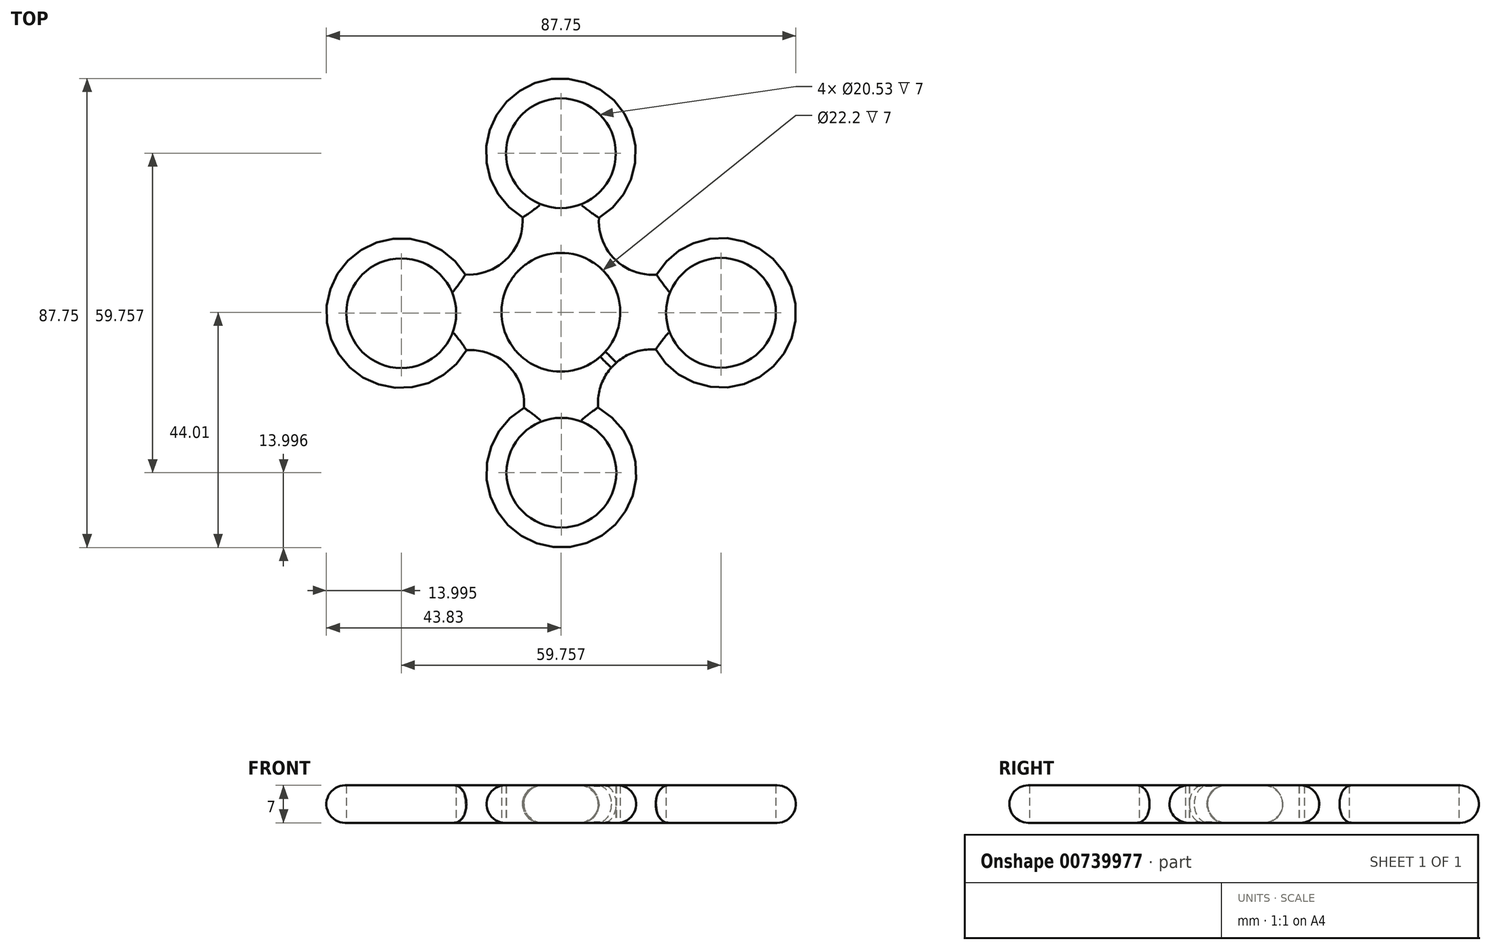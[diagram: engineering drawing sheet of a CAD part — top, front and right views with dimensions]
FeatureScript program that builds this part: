
annotation { "Feature Type Name" : "Feature", "Feature Type Description" : "" }
export const myFeature = defineFeature(function(context is Context, id is Id, definition is map)
    precondition{}
    {
        {
            var Q0;
            Q0=qCreatedBy(makeId("Top.planeOp"),FACE);
            var sketch = newSketch(context, id + "F0", { "sketchPlane" : qUnion([Q0])});
            skCircle(sketch, "E0", {"center": v(0, 0) * mm, "radius": 11.1 * mm});
            skLineSegment(sketch, "E1", {"start": v(0, 11.1) * mm, "end": v(0, 16.1) * mm});
            skCircle(sketch, "E2", {"center": v(0, 29.74) * mm, "radius": 10.26 * mm});
            skCircle(sketch, "E3.1.0", {"center": v(-29.83, -0.18) * mm, "radius": 10.26 * mm});
            skCircle(sketch, "E3.2.0", {"center": v(0.09, -30.01) * mm, "radius": 10.26 * mm});
            skCircle(sketch, "E3.3.0", {"center": v(29.92, -0.1) * mm, "radius": 10.26 * mm});
            skPoint(sketch, "E3.center", {"position": v(0.04, -0.14) * mm});
            skCircle(sketch, "E4", {"center": v(0, 29.74) * mm, "radius": 14 * mm});
            skCircle(sketch, "E5", {"center": v(29.92, -0.1) * mm, "radius": 14 * mm});
            skCircle(sketch, "E6", {"center": v(0.09, -30.01) * mm, "radius": 14 * mm});
            skCircle(sketch, "E7", {"center": v(-29.83, -0.18) * mm, "radius": 14 * mm});
            skCircle(sketch, "E8", {"center": v(0, 0) * mm, "radius": 14 * mm});
            skArc(sketch, "E9", {"start": v(-6.91, -17.9) * mm, "mid": v(-9.8, -10.02) * mm, "end": v(-17.66, -7.09) * mm});
            skArc(sketch, "E10", {"start": v(-17.85, 7.06) * mm, "mid": v(-10.1, 9.97) * mm, "end": v(-7.18, 17.72) * mm});
            skArc(sketch, "E11", {"start": v(7.11, 17.69) * mm, "mid": v(10.07, 9.92) * mm, "end": v(17.88, 7.05) * mm});
            skArc(sketch, "E12", {"start": v(17.73, -6.97) * mm, "mid": v(9.84, -9.9) * mm, "end": v(6.96, -17.82) * mm});
            skArc(sketch, "E13.trimOffspring", {"start": v(10.14, -27.96) * mm, "mid": v(11.9, -27.26) * mm, "end": v(13.62, -26.44) * mm});
            skSolve(sketch);
        }
        {
            var Q0;
            Q0 = qSketchRegion(id + "F0", true);
            extrude(context, id + "F1", {"entities" : qUnion([Q0]), "depth" : 7 * mm, "offsetDistance" : 25 * mm});
        }
        {
            var Q0;
            {var subQ0=sQuery(id+"F0.wireOp",EDGE,"E12");Q0=makeQuery(id+"F1.opExtrude","CAP_EDGE",EDGE,{"disambiguationData":[OSD([subQ0]),TDD([makeQuery(id+"F0.imprint","IMPRINT",EDGE,{"disambiguationData":[TD([[makeQuery(id+"F0.imprint","INTERSECT",VERTEX,{"derivedFrom":[sQuery(id+"F0.wireOp",EDGE,"E5"),subQ0]}),-1.0]])],"derivedFrom":subQ0})])],"isStart":true});}
            var Q1;
            Q1=makeQuery(id+"F1.opExtrude","CAP_EDGE",EDGE,{"disambiguationData":[OSD([sQuery(id+"F0.wireOp",EDGE,"E5")])],"isStart":true});
            var Q2;
            {var subQ0=sQuery(id+"F0.wireOp",EDGE,"E12");Q2=makeQuery(id+"F1.opExtrude","CAP_EDGE",EDGE,{"disambiguationData":[OSD([subQ0]),TDD([makeQuery(id+"F0.imprint","IMPRINT",EDGE,{"disambiguationData":[TD([[makeQuery(id+"F0.imprint","INTERSECT",VERTEX,{"derivedFrom":[sQuery(id+"F0.wireOp",EDGE,"E6"),subQ0]}),1.0]])],"derivedFrom":subQ0})])],"isStart":true});}
            var Q3;
            Q3=makeQuery(id+"F1.opExtrude","CAP_EDGE",EDGE,{"disambiguationData":[OSD([sQuery(id+"F0.wireOp",EDGE,"E8")])],"isStart":true});
            var Q4;
            Q4=makeQuery(id+"F1.opExtrude","CAP_EDGE",EDGE,{"disambiguationData":[OSD([sQuery(id+"F0.wireOp",EDGE,"E6")])],"isStart":true});
            var Q5;
            Q5=makeQuery(id+"F1.opExtrude","CAP_EDGE",EDGE,{"disambiguationData":[OSD([sQuery(id+"F0.wireOp",EDGE,"E9")])],"isStart":true});
            var Q6;
            Q6=makeQuery(id+"F1.opExtrude","CAP_EDGE",EDGE,{"disambiguationData":[OSD([sQuery(id+"F0.wireOp",EDGE,"E7")])],"isStart":true});
            var Q7;
            Q7=makeQuery(id+"F1.opExtrude","CAP_EDGE",EDGE,{"disambiguationData":[OSD([sQuery(id+"F0.wireOp",EDGE,"E10")])],"isStart":true});
            var Q8;
            Q8=makeQuery(id+"F1.opExtrude","CAP_EDGE",EDGE,{"disambiguationData":[OSD([sQuery(id+"F0.wireOp",EDGE,"E11")])],"isStart":false});
            var Q9;
            Q9=makeQuery(id+"F1.opExtrude","CAP_EDGE",EDGE,{"disambiguationData":[OSD([sQuery(id+"F0.wireOp",EDGE,"E4")])],"isStart":false});
            var Q10;
            Q10=makeQuery(id+"F1.opExtrude","CAP_EDGE",EDGE,{"disambiguationData":[OSD([sQuery(id+"F0.wireOp",EDGE,"E4")])],"isStart":true});
            var Q11;
            Q11=makeQuery(id+"F1.opExtrude","CAP_EDGE",EDGE,{"disambiguationData":[OSD([sQuery(id+"F0.wireOp",EDGE,"E11")])],"isStart":true});
            var Q12;
            Q12=makeQuery(id+"F1.opExtrude","CAP_EDGE",EDGE,{"disambiguationData":[OSD([sQuery(id+"F0.wireOp",EDGE,"E5")])],"isStart":false});
            var Q13;
            Q13=makeQuery(id+"F1.opExtrude","CAP_EDGE",EDGE,{"disambiguationData":[OSD([sQuery(id+"F0.wireOp",EDGE,"E10")])],"isStart":false});
            var Q14;
            Q14=makeQuery(id+"F1.opExtrude","CAP_EDGE",EDGE,{"disambiguationData":[OSD([sQuery(id+"F0.wireOp",EDGE,"E7")])],"isStart":false});
            var Q15;
            Q15=makeQuery(id+"F1.opExtrude","CAP_EDGE",EDGE,{"disambiguationData":[OSD([sQuery(id+"F0.wireOp",EDGE,"E6")])],"isStart":false});
            var Q16;
            Q16=makeQuery(id+"F1.opExtrude","CAP_EDGE",EDGE,{"disambiguationData":[OSD([sQuery(id+"F0.wireOp",EDGE,"E9")])],"isStart":false});
            var Q17;
            {var subQ0=sQuery(id+"F0.wireOp",EDGE,"E12");Q17=makeQuery(id+"F1.opExtrude","CAP_EDGE",EDGE,{"disambiguationData":[OSD([subQ0]),TDD([makeQuery(id+"F0.imprint","IMPRINT",EDGE,{"disambiguationData":[TD([[makeQuery(id+"F0.imprint","INTERSECT",VERTEX,{"derivedFrom":[sQuery(id+"F0.wireOp",EDGE,"E6"),subQ0]}),1.0]])],"derivedFrom":subQ0})])],"isStart":false});}
            var Q18;
            {var subQ0=sQuery(id+"F0.wireOp",EDGE,"E12");Q18=makeQuery(id+"F1.opExtrude","CAP_EDGE",EDGE,{"disambiguationData":[OSD([subQ0]),TDD([makeQuery(id+"F0.imprint","IMPRINT",EDGE,{"disambiguationData":[TD([[makeQuery(id+"F0.imprint","INTERSECT",VERTEX,{"derivedFrom":[sQuery(id+"F0.wireOp",EDGE,"E5"),subQ0]}),-1.0]])],"derivedFrom":subQ0})])],"isStart":false});}
            var Q19;
            Q19=makeQuery(id+"F1.opExtrude","CAP_EDGE",EDGE,{"disambiguationData":[OSD([sQuery(id+"F0.wireOp",EDGE,"E8")])],"isStart":false});
            fillet(context, id + "F2", {"entities" : qUnion([Q0, Q1, Q2, Q3, Q4, Q5, Q6, Q7, Q8, Q9, Q10, Q11, Q12, Q13, Q14, Q15, Q16, Q17, Q18, Q19]), "radius" : 3.5 * mm, "tangentPropagation" : true, "defaultsChanged" : false, "vertexSettings" : [], "allowEdgeOverflow" : false});
        }
    });
